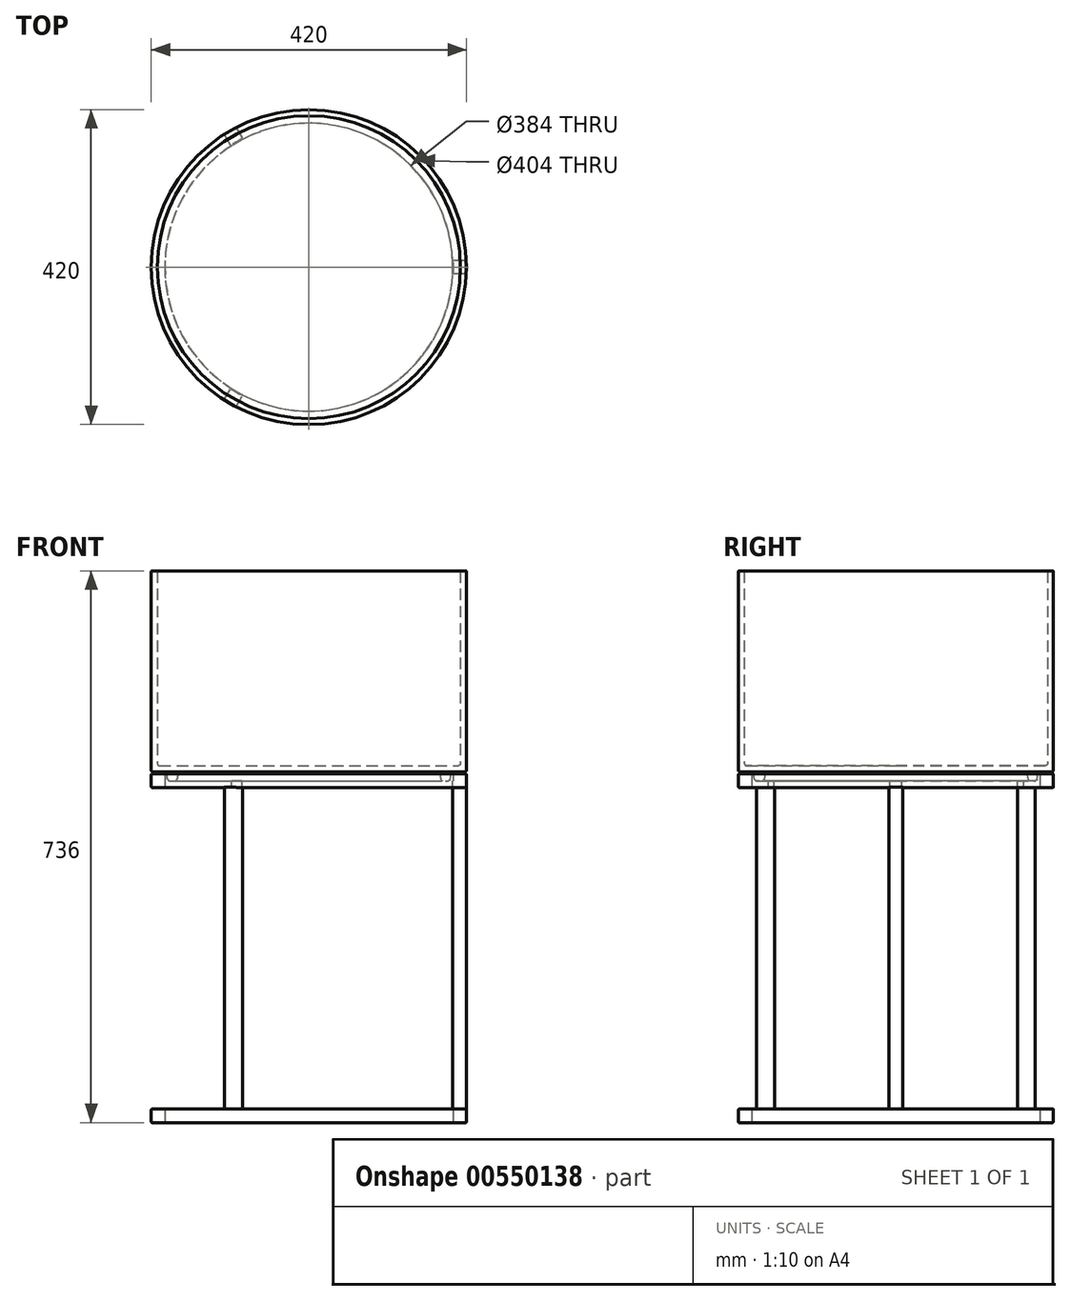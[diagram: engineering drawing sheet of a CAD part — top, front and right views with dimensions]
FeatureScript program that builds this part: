
annotation { "Feature Type Name" : "Feature", "Feature Type Description" : "" }
export const myFeature = defineFeature(function(context is Context, id is Id, definition is map)
    precondition{}
    {
        {
            var Q0;
            Q0=qCreatedBy(makeId("Front.planeOp"),FACE);
            var sketch = newSketch(context, id + "F0", { "sketchPlane" : qUnion([Q0])});
            skLineSegment(sketch, "E0", {"start": v(0, 0) * mm, "end": v(210, 0) * mm, "construction": true});
            skLineSegment(sketch, "E1", {"start": v(209, 280) * mm, "end": v(203, 280) * mm});
            skLineSegment(sketch, "E2", {"start": v(202, 279) * mm, "end": v(202, 23) * mm});
            skLineSegment(sketch, "E3", {"start": v(199, 20) * mm, "end": v(0, 20) * mm});
            skLineSegment(sketch, "E4", {"start": v(0, 20) * mm, "end": v(0, 12) * mm});
            skLineSegment(sketch, "E5", {"start": v(0, 12) * mm, "end": v(172.32, 12) * mm});
            skLineSegment(sketch, "E6", {"start": v(174.3, 10.35) * mm, "end": v(175.82, 1.65) * mm});
            skLineSegment(sketch, "E7", {"start": v(177.8, 0) * mm, "end": v(186.2, 0) * mm});
            skLineSegment(sketch, "E8", {"start": v(188.18, 1.65) * mm, "end": v(189.7, 10.35) * mm});
            skLineSegment(sketch, "E9", {"start": v(191.68, 12) * mm, "end": v(208, 12) * mm});
            skLineSegment(sketch, "E10", {"start": v(210, 14) * mm, "end": v(210, 279) * mm});
            skPoint(sketch, "E11.visualSharp", {"position": v(202, 20) * mm});
            skArc(sketch, "E11.filletArc", {"start": v(199, 20) * mm, "mid": v(201.12, 20.88) * mm, "end": v(202, 23) * mm});
            skPoint(sketch, "E12.visualSharp", {"position": v(210, 12) * mm});
            skArc(sketch, "E12.filletArc", {"start": v(208, 12) * mm, "mid": v(209.41, 12.59) * mm, "end": v(210, 14) * mm});
            skPoint(sketch, "E13.visualSharp", {"position": v(190, 12) * mm});
            skArc(sketch, "E13.filletArc", {"start": v(191.68, 12) * mm, "mid": v(190.4, 11.53) * mm, "end": v(189.7, 10.35) * mm});
            skPoint(sketch, "E14.visualSharp", {"position": v(174, 12) * mm});
            skArc(sketch, "E14.filletArc", {"start": v(174.3, 10.35) * mm, "mid": v(173.6, 11.53) * mm, "end": v(172.32, 12) * mm});
            skPoint(sketch, "E15.visualSharp", {"position": v(187.88, 0) * mm});
            skArc(sketch, "E15.filletArc", {"start": v(186.2, 0) * mm, "mid": v(187.5, 0.47) * mm, "end": v(188.18, 1.65) * mm});
            skPoint(sketch, "E16.visualSharp", {"position": v(176.12, 0) * mm});
            skArc(sketch, "E16.filletArc", {"start": v(175.82, 1.65) * mm, "mid": v(176.5, 0.47) * mm, "end": v(177.8, 0) * mm});
            skPoint(sketch, "E17.visualSharp", {"position": v(210, 280) * mm});
            skArc(sketch, "E17.filletArc", {"start": v(210, 279) * mm, "mid": v(209.7, 279.7) * mm, "end": v(209, 280) * mm});
            skPoint(sketch, "E18.visualSharp", {"position": v(202, 280) * mm});
            skArc(sketch, "E18.filletArc", {"start": v(203, 280) * mm, "mid": v(202.3, 279.7) * mm, "end": v(202, 279) * mm});
            skLineSegment(sketch, "E19", {"start": v(0, 0) * mm, "end": v(0, 20) * mm, "construction": true});
            skSolve(sketch);
        }
        {
            var Q0;
            Q0=makeQuery(id+"F0.imprint","IMPRINT",FACE,{"disambiguationData":[TD([[makeQuery(id+"F0.imprint","IMPRINT",EDGE,{"derivedFrom":sQuery(id+"F0.wireOp",EDGE,"E1")}),1.0]])]});
            var Q1;
            Q1=sQuery(id+"F0.wireOp",EDGE,"E19");
            revolve(context, id + "F1", {"entities" : qUnion([Q0]), "axis" : qUnion([Q1]), "revolveType" : RevolveType.FULL});
        }
        {
            var Q0;
            Q0=qCreatedBy(makeId("Front.planeOp"),FACE);
            var sketch = newSketch(context, id + "F2", { "sketchPlane" : qUnion([Q0])});
            skLineSegment(sketch, "E20.bottom", {"start": v(209, -9) * mm, "end": v(193, -9) * mm});
            skLineSegment(sketch, "E20.top", {"start": v(209, 9) * mm, "end": v(193, 9) * mm});
            skLineSegment(sketch, "E20.left", {"start": v(210, -8) * mm, "end": v(210, 8) * mm});
            skLineSegment(sketch, "E20.right", {"start": v(192, -8) * mm, "end": v(192, 8) * mm});
            skPoint(sketch, "E21.visualSharp", {"position": v(192, 9) * mm});
            skArc(sketch, "E21.filletArc", {"start": v(193, 9) * mm, "mid": v(192.3, 8.7) * mm, "end": v(192, 8) * mm});
            skPoint(sketch, "E22.visualSharp", {"position": v(210, 9) * mm});
            skArc(sketch, "E22.filletArc", {"start": v(210, 8) * mm, "mid": v(209.7, 8.7) * mm, "end": v(209, 9) * mm});
            skArc(sketch, "E23.filletArc", {"start": v(209, -9) * mm, "mid": v(209.7, -8.7) * mm, "end": v(210, -8) * mm});
            skPoint(sketch, "E24.visualSharp", {"position": v(192, -9) * mm});
            skArc(sketch, "E24.filletArc", {"start": v(192, -8) * mm, "mid": v(192.3, -8.7) * mm, "end": v(193, -9) * mm});
            skLineSegment(sketch, "E25", {"start": v(0, 0) * mm, "end": v(0, 20) * mm, "construction": true});
            skPoint(sketch, "E26", {"position": v(210, 0) * mm});
            skSolve(sketch);
        }
        {
            var Q0;
            Q0 = qSketchRegion(id + "F2", true);
            var Q1;
            Q1=sQuery(id+"F2.wireOp",EDGE,"E25");
            revolve(context, id + "F3", {"operationType" : NewBodyOperationType.ADD, "entities" : qUnion([Q0]), "axis" : qUnion([Q1]), "revolveType" : RevolveType.FULL});
        }
        {
            var Q0;
            Q0=qCreatedBy(makeId("Top.planeOp"),FACE);
            var sketch = newSketch(context, id + "F4", { "sketchPlane" : qUnion([Q0])});
            skLineSegment(sketch, "E27.bottom", {"start": v(208.8, -9) * mm, "end": v(192.8, -9) * mm});
            skLineSegment(sketch, "E27.top", {"start": v(208.8, 9) * mm, "end": v(192.8, 9) * mm});
            skLineSegment(sketch, "E27.left", {"start": v(209.8, -8) * mm, "end": v(209.8, 8) * mm});
            skLineSegment(sketch, "E27.right", {"start": v(191.8, -8) * mm, "end": v(191.8, 8) * mm});
            skPoint(sketch, "E27.middle", {"position": v(200.8, 0) * mm});
            skPoint(sketch, "E28", {"position": v(209.8, 0) * mm});
            skPoint(sketch, "E29.visualSharp", {"position": v(209.8, -9) * mm});
            skArc(sketch, "E29.filletArc", {"start": v(208.8, -9) * mm, "mid": v(209.51, -8.7) * mm, "end": v(209.8, -8) * mm});
            skPoint(sketch, "E30.visualSharp", {"position": v(209.8, 9) * mm});
            skArc(sketch, "E30.filletArc", {"start": v(209.8, 8) * mm, "mid": v(209.51, 8.7) * mm, "end": v(208.8, 9) * mm});
            skPoint(sketch, "E31.visualSharp", {"position": v(191.8, -9) * mm});
            skArc(sketch, "E31.filletArc", {"start": v(191.8, -8) * mm, "mid": v(192.1, -8.7) * mm, "end": v(192.8, -9) * mm});
            skPoint(sketch, "E32.visualSharp", {"position": v(191.8, 9) * mm});
            skArc(sketch, "E32.filletArc", {"start": v(192.8, 9) * mm, "mid": v(192.1, 8.7) * mm, "end": v(191.8, 8) * mm});
            skLineSegment(sketch, "E33.1.0", {"start": v(-96.6, 185.33) * mm, "end": v(-88.6, 171.48) * mm});
            skArc(sketch, "E33.1.1", {"start": v(-96.6, 185.33) * mm, "mid": v(-97.22, 185.8) * mm, "end": v(-97.97, 185.7) * mm});
            skLineSegment(sketch, "E33.1.2", {"start": v(-97.97, 185.7) * mm, "end": v(-111.83, 177.7) * mm});
            skArc(sketch, "E33.1.3", {"start": v(-111.83, 177.7) * mm, "mid": v(-112.3, 177.1) * mm, "end": v(-112.2, 176.33) * mm});
            skLineSegment(sketch, "E33.1.4", {"start": v(-112.2, 176.33) * mm, "end": v(-104.2, 162.48) * mm});
            skArc(sketch, "E33.1.5", {"start": v(-104.2, 162.48) * mm, "mid": v(-103.6, 162) * mm, "end": v(-102.83, 162.1) * mm});
            skLineSegment(sketch, "E33.1.6", {"start": v(-88.97, 170.1) * mm, "end": v(-102.83, 162.1) * mm});
            skArc(sketch, "E33.1.7", {"start": v(-88.97, 170.1) * mm, "mid": v(-88.5, 170.72) * mm, "end": v(-88.6, 171.48) * mm});
            skLineSegment(sketch, "E33.2.0", {"start": v(-112.2, -176.33) * mm, "end": v(-104.2, -162.48) * mm});
            skArc(sketch, "E33.2.1", {"start": v(-112.2, -176.33) * mm, "mid": v(-112.3, -177.1) * mm, "end": v(-111.83, -177.7) * mm});
            skLineSegment(sketch, "E33.2.2", {"start": v(-111.83, -177.7) * mm, "end": v(-97.97, -185.7) * mm});
            skArc(sketch, "E33.2.3", {"start": v(-97.97, -185.7) * mm, "mid": v(-97.22, -185.8) * mm, "end": v(-96.6, -185.33) * mm});
            skLineSegment(sketch, "E33.2.4", {"start": v(-96.6, -185.33) * mm, "end": v(-88.6, -171.48) * mm});
            skArc(sketch, "E33.2.5", {"start": v(-88.6, -171.48) * mm, "mid": v(-88.5, -170.72) * mm, "end": v(-88.97, -170.1) * mm});
            skLineSegment(sketch, "E33.2.6", {"start": v(-102.83, -162.1) * mm, "end": v(-88.97, -170.1) * mm});
            skArc(sketch, "E33.2.7", {"start": v(-102.83, -162.1) * mm, "mid": v(-103.6, -162) * mm, "end": v(-104.2, -162.48) * mm});
            skPoint(sketch, "E33.center", {"position": v(0, 0) * mm});
            skSolve(sketch);
        }
        {
            var Q0;
            Q0 = qSketchRegion(id + "F4", true);
            extrude(context, id + "F5", {"entities" : qUnion([Q0]), "operationType" : NewBodyOperationType.ADD, "oppositeDirection" : true, "depth" : ((300 * 1.5) - 12) * mm, "offsetDistance" : 25 * mm});
        }
        {
            var Q0;
            Q0=qCreatedBy(makeId("Front.planeOp"),FACE);
            var sketch = newSketch(context, id + "F6", { "sketchPlane" : qUnion([Q0])});
            skLineSegment(sketch, "E34.bottom", {"start": v(209, -456) * mm, "end": v(193, -456) * mm});
            skLineSegment(sketch, "E34.top", {"start": v(209, -438) * mm, "end": v(193, -438) * mm});
            skLineSegment(sketch, "E34.left", {"start": v(210, -455) * mm, "end": v(210, -439) * mm});
            skLineSegment(sketch, "E34.right", {"start": v(192, -455) * mm, "end": v(192, -439) * mm});
            skPoint(sketch, "E35.visualSharp", {"position": v(192, -438) * mm});
            skArc(sketch, "E35.filletArc", {"start": v(193, -438) * mm, "mid": v(192.3, -438.3) * mm, "end": v(192, -439) * mm});
            skPoint(sketch, "E36.visualSharp", {"position": v(210, -438) * mm});
            skArc(sketch, "E36.filletArc", {"start": v(210, -439) * mm, "mid": v(209.7, -438.3) * mm, "end": v(209, -438) * mm});
            skArc(sketch, "E37.filletArc", {"start": v(209, -456) * mm, "mid": v(209.7, -455.7) * mm, "end": v(210, -455) * mm});
            skPoint(sketch, "E38.visualSharp", {"position": v(192, -456) * mm});
            skArc(sketch, "E38.filletArc", {"start": v(192, -455) * mm, "mid": v(192.3, -455.7) * mm, "end": v(193, -456) * mm});
            skPoint(sketch, "E39", {"position": v(210, -447) * mm});
            skSolve(sketch);
        }
        {
            var Q0;
            Q0 = qSketchRegion(id + "F6", true);
            var Q1;
            Q1=sQuery(id+"F2.wireOp",EDGE,"E25");
            revolve(context, id + "F7", {"operationType" : NewBodyOperationType.ADD, "entities" : qUnion([Q0]), "axis" : qUnion([Q1]), "revolveType" : RevolveType.FULL});
        }
    });
